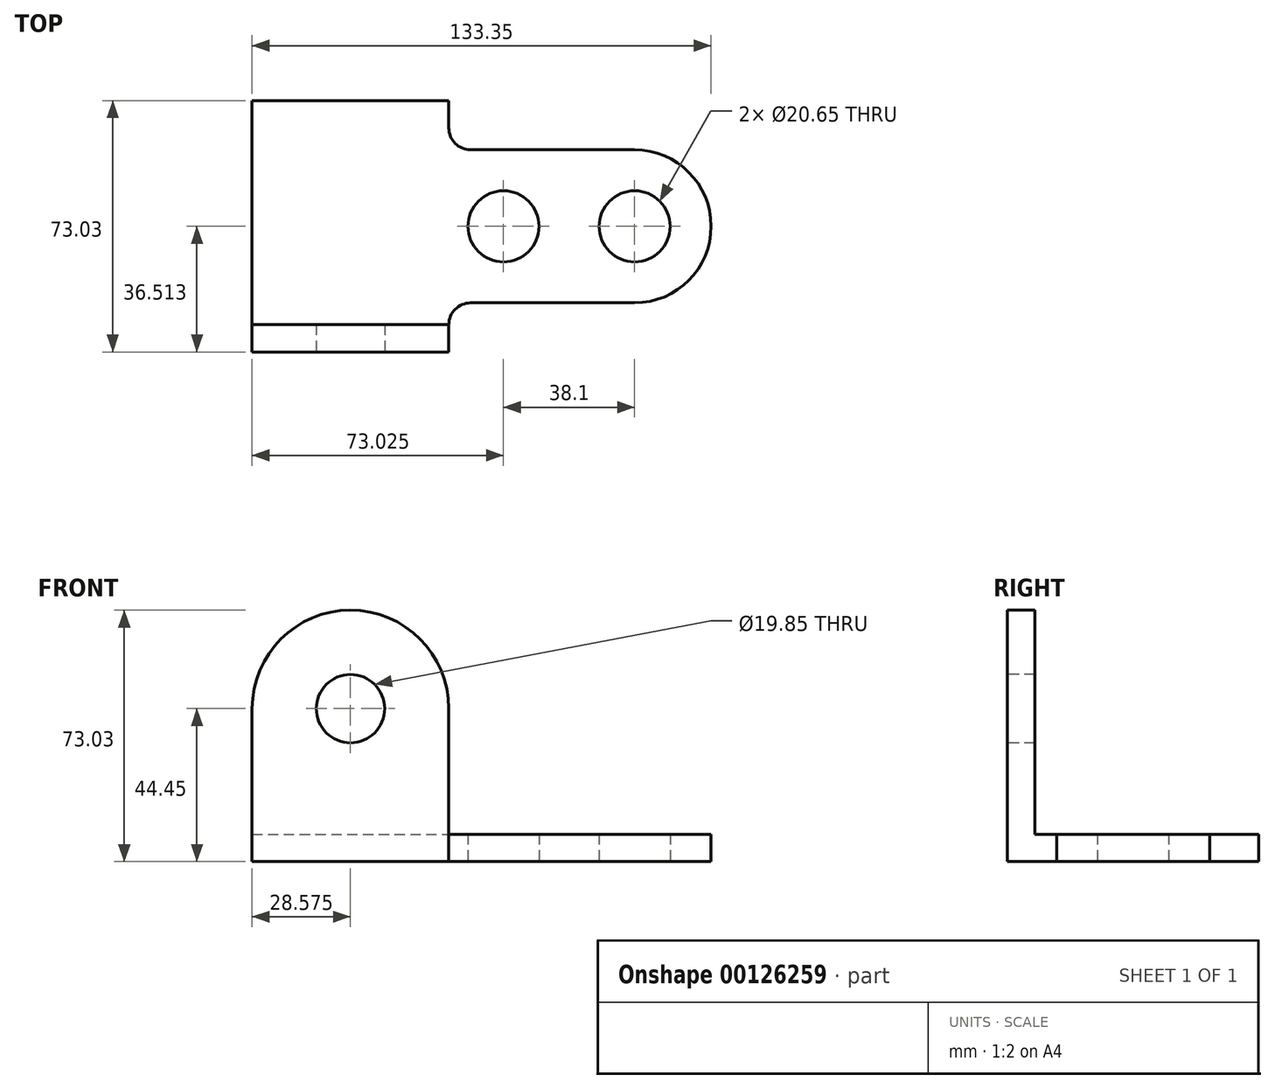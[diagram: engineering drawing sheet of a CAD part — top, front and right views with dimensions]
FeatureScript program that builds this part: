
annotation { "Feature Type Name" : "Feature", "Feature Type Description" : "" }
export const myFeature = defineFeature(function(context is Context, id is Id, definition is map)
    precondition{}
    {
        {
            var Q0;
            Q0=qCreatedBy(makeId("Top.planeOp"),FACE);
            var sketch = newSketch(context, id + "F0", { "sketchPlane" : qUnion([Q0])});
            skLineSegment(sketch, "E0.bottom", {"start": v(0, 0) * mm, "end": v(57.15, 0) * mm});
            skLineSegment(sketch, "E0.top", {"start": v(0, 73.03) * mm, "end": v(57.15, 73.03) * mm});
            skLineSegment(sketch, "E0.left", {"start": v(0, 0) * mm, "end": v(0, 73.03) * mm});
            skLineSegment(sketch, "E1", {"start": v(57.15, 0) * mm, "end": v(57.15, 14.29) * mm});
            skLineSegment(sketch, "E2", {"start": v(57.15, 80.83) * mm, "end": v(57.15, 73.03) * mm});
            skCircle(sketch, "E3", {"center": v(111.12, 36.51) * mm, "radius": 10.33 * mm});
            skCircle(sketch, "E4", {"center": v(73.03, 36.51) * mm, "radius": 10.33 * mm});
            skLineSegment(sketch, "E5", {"start": v(57.15, 73.03) * mm, "end": v(57.15, 58.74) * mm});
            skLineSegment(sketch, "E6.bottom", {"start": v(57.15, 14.29) * mm, "end": v(111.12, 14.29) * mm});
            skLineSegment(sketch, "E6.top", {"start": v(57.15, 58.74) * mm, "end": v(111.12, 58.74) * mm});
            skArc(sketch, "E7", {"start": v(111.12, 14.29) * mm, "mid": v(133.35, 36.51) * mm, "end": v(111.12, 58.74) * mm});
            skSolve(sketch);
        }
        {
            var Q0;
            Q0 = qSketchRegion(id + "F0", true);
            extrude(context, id + "F1", {"entities" : qUnion([Q0]), "depth" : 7.94 * mm});
        }
        {
            var Q0;
            Q0=qCreatedBy(makeId("Front.planeOp"),FACE);
            var sketch = newSketch(context, id + "F2", { "sketchPlane" : qUnion([Q0])});
            skLineSegment(sketch, "E8.bottom", {"start": v(0, 0) * mm, "end": v(57.15, 0) * mm});
            skLineSegment(sketch, "E8.left", {"start": v(0, 0) * mm, "end": v(0, 44.45) * mm});
            skLineSegment(sketch, "E8.right", {"start": v(57.15, 0) * mm, "end": v(57.15, 44.45) * mm});
            skArc(sketch, "E9", {"start": v(57.15, 44.45) * mm, "mid": v(28.58, 73.03) * mm, "end": v(0, 44.45) * mm});
            skCircle(sketch, "E10", {"center": v(28.58, 44.45) * mm, "radius": 9.92 * mm});
            skSolve(sketch);
        }
        {
            var Q0;
            Q0 = qSketchRegion(id + "F2", true);
            extrude(context, id + "F3", {"entities" : qUnion([Q0]), "operationType" : NewBodyOperationType.ADD, "oppositeDirection" : true, "depth" : 7.94 * mm});
        }
        {
            var Q0;
            Q0=makeQuery(id+"F1.opExtrude","SWEPT_EDGE",EDGE,{"disambiguationData":[OSD([sQuery(id+"F0.wireOp",EDGE,"E1"),sQuery(id+"F0.wireOp",EDGE,"E6.bottom")])]});
            var Q1;
            Q1=makeQuery(id+"F1.opExtrude","SWEPT_EDGE",EDGE,{"disambiguationData":[OSD([sQuery(id+"F0.wireOp",EDGE,"E5"),sQuery(id+"F0.wireOp",EDGE,"E6.top")])]});
            fillet(context, id + "F4", {"entities" : qUnion([Q0, Q1]), "radius" : 6.35 * mm, "tangentPropagation" : true, "allowEdgeOverflow" : false});
        }
        {
            var Q0;
            Q0=makeQuery(id+"F1.opExtrude","SWEPT_FACE",FACE,{"disambiguationData":[OSD([sQuery(id+"F0.wireOp",EDGE,"E6.top")])]});
            var Q1;
            Q1=makeQuery(id+"F1.opExtrude","SWEPT_FACE",FACE,{"disambiguationData":[OSD([sQuery(id+"F0.wireOp",EDGE,"E6.bottom")])]});
            cPlane(context, id + "F5", {"entities" : qUnion([Q0, Q1]), "cplaneType" : CPlaneType.MID_PLANE, "offset" : 25.4 * mm, "width" : 152.4 * mm, "height" : 152.4 * mm});
        }
    });
